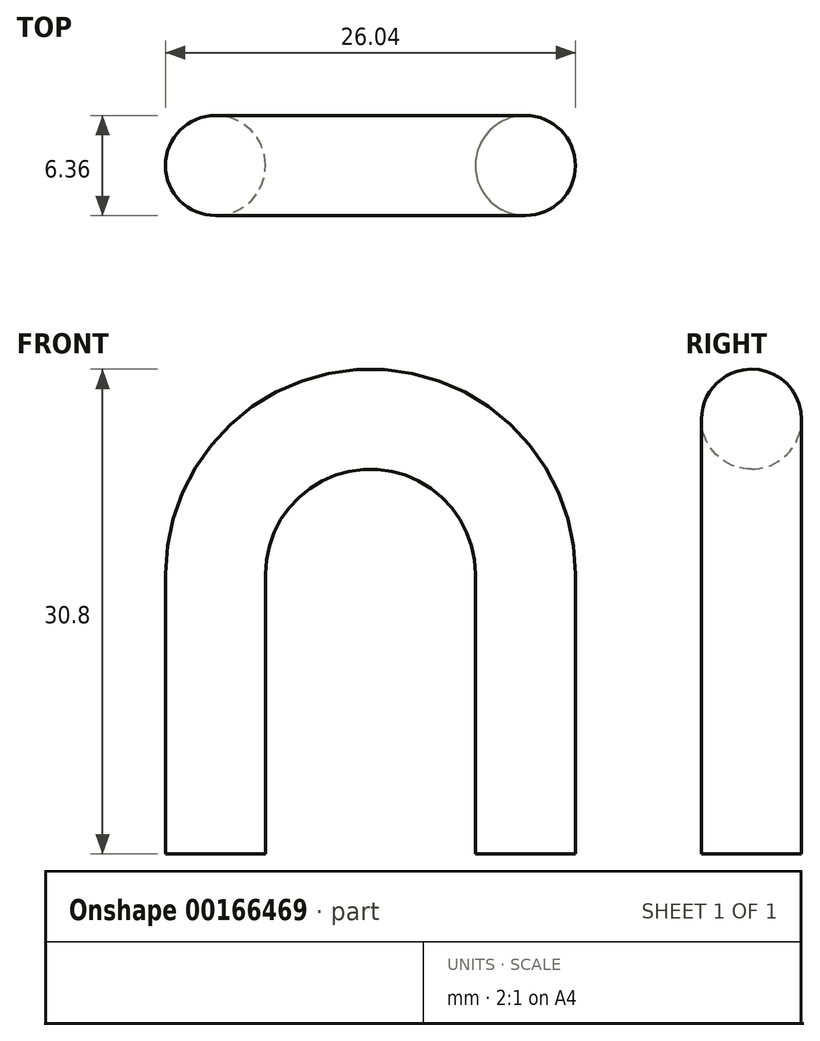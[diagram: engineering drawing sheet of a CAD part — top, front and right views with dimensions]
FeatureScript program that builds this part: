
annotation { "Feature Type Name" : "Feature", "Feature Type Description" : "" }
export const myFeature = defineFeature(function(context is Context, id is Id, definition is map)
    precondition{}
    {
        {
            var Q0;
            Q0=qCreatedBy(makeId("Front.planeOp"),FACE);
            var sketch = newSketch(context, id + "F0", { "sketchPlane" : qUnion([Q0])});
            skLineSegment(sketch, "E0", {"start": v(9.84, 0) * mm, "end": v(9.84, 17.78) * mm});
            skArc(sketch, "E1", {"start": v(9.84, 17.78) * mm, "mid": v(0, 27.62) * mm, "end": v(-9.84, 17.78) * mm});
            skLineSegment(sketch, "E2", {"start": v(-9.84, 17.78) * mm, "end": v(-9.84, 0) * mm});
            skSolve(sketch);
        }
        {
            var Q0;
            Q0=qCreatedBy(makeId("Top.planeOp"),FACE);
            var sketch = newSketch(context, id + "F1", { "sketchPlane" : qUnion([Q0])});
            skCircle(sketch, "E3", {"center": v(-9.84, 0) * mm, "radius": 3.18 * mm});
            skSolve(sketch);
        }
        {
            var Q0;
            Q0=makeQuery(id+"F1.imprint","IMPRINT",FACE,{"disambiguationData":[TD([[makeQuery(id+"F1.imprint","IMPRINT",EDGE,{"derivedFrom":sQuery(id+"F1.wireOp",EDGE,"E3")}),1.0]])]});
            var Q1;
            Q1=sQuery(id+"F0.wireOp",EDGE,"E1");
            var Q2;
            Q2=sQuery(id+"F0.wireOp",EDGE,"E2");
            var Q3;
            Q3=sQuery(id+"F0.wireOp",EDGE,"E0");
            sweep(context, id + "F2", {"profiles" : qUnion([Q0]), "path" : qUnion([Q1, Q2, Q3])});
        }
    });
